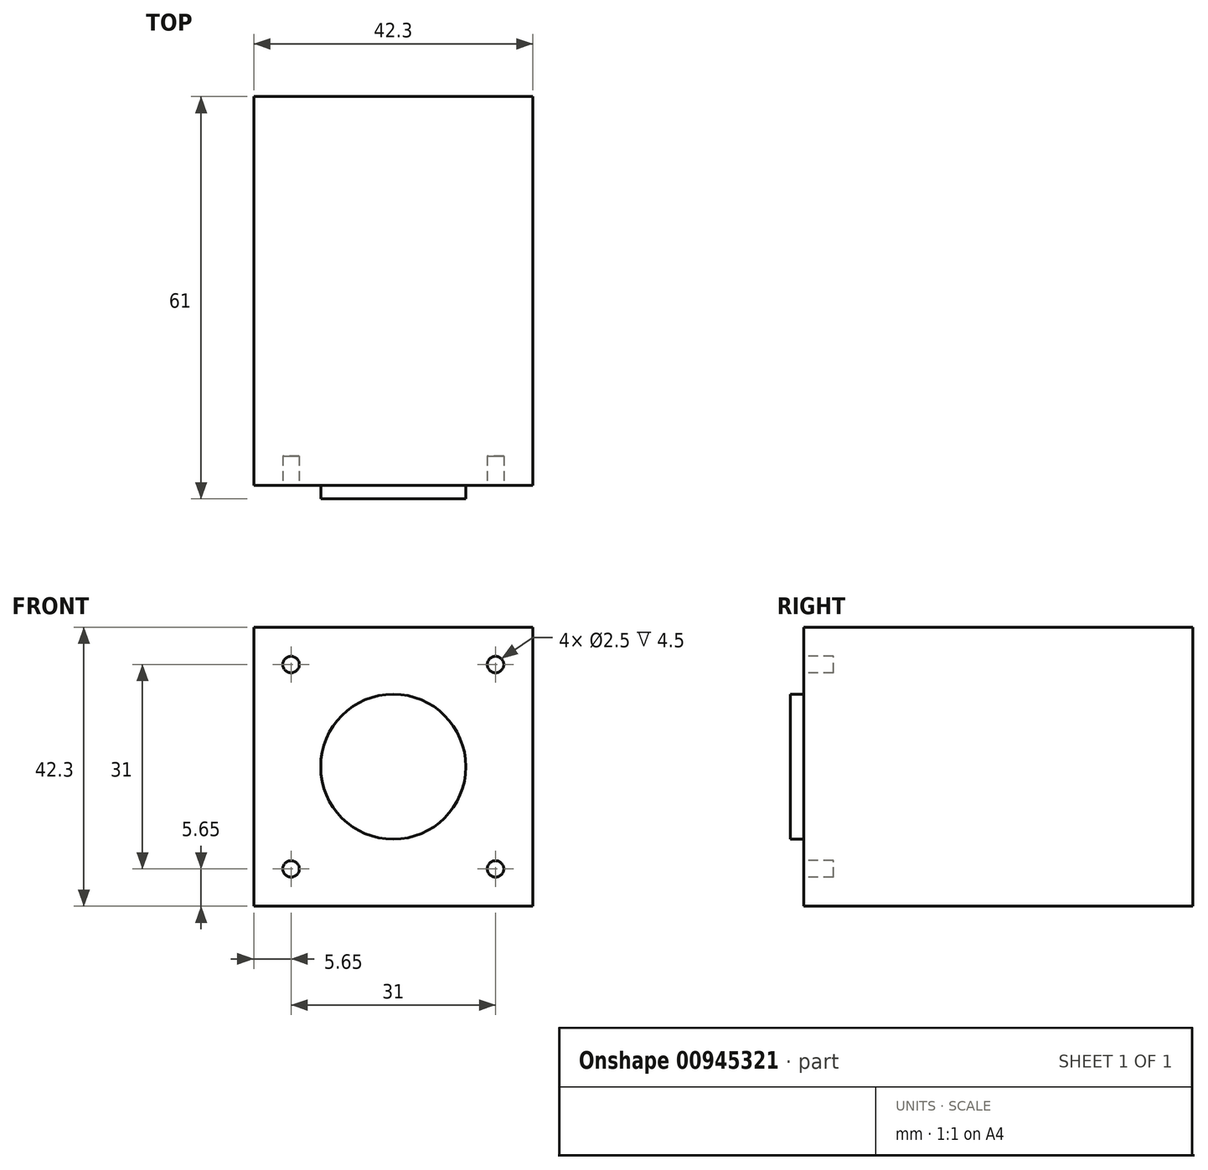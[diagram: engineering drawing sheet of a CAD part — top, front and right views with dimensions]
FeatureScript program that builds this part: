
annotation { "Feature Type Name" : "Feature", "Feature Type Description" : "" }
export const myFeature = defineFeature(function(context is Context, id is Id, definition is map)
    precondition{}
    {
        {
            var Q0;
            Q0=qCreatedBy(makeId("Front.planeOp"),FACE);
            var sketch = newSketch(context, id + "F0", { "sketchPlane" : qUnion([Q0])});
            skLineSegment(sketch, "E0.bottom", {"start": v(-21.15, 21.15) * mm, "end": v(21.15, 21.15) * mm});
            skLineSegment(sketch, "E0.top", {"start": v(-21.15, -21.15) * mm, "end": v(21.15, -21.15) * mm});
            skLineSegment(sketch, "E0.left", {"start": v(-21.15, 21.15) * mm, "end": v(-21.15, -21.15) * mm});
            skLineSegment(sketch, "E0.right", {"start": v(21.15, 21.15) * mm, "end": v(21.15, -21.15) * mm});
            skPoint(sketch, "E1", {"position": v(0, 0) * mm});
            skSolve(sketch);
        }
        {
            var Q0;
            Q0=makeQuery(id+"F0.imprint","IMPRINT",FACE,{"disambiguationData":[TD([[makeQuery(id+"F0.imprint","IMPRINT",EDGE,{"derivedFrom":sQuery(id+"F0.wireOp",EDGE,"E0.bottom")}),-1.0]])]});
            extrude(context, id + "F1", {"entities" : qUnion([Q0]), "depth" : 59 * mm});
        }
        {
            var Q0;
            Q0=makeQuery(id+"F1.opExtrude","CAP_FACE",FACE,{"disambiguationData":[OSD([sQuery(id+"F0.wireOp",EDGE,"E0.bottom"),sQuery(id+"F0.wireOp",EDGE,"E0.top"),sQuery(id+"F0.wireOp",EDGE,"E0.left"),sQuery(id+"F0.wireOp",EDGE,"E0.right")])],"isStart":false});
            var sketch = newSketch(context, id + "F2", { "sketchPlane" : qUnion([Q0])});
            skCircle(sketch, "E2", {"center": v(0, 0) * mm, "radius": 11 * mm});
            skSolve(sketch);
        }
        {
            var Q0;
            Q0=makeQuery(id+"F2.imprint","IMPRINT",FACE,{"disambiguationData":[TD([[makeQuery(id+"F2.imprint","IMPRINT",EDGE,{"derivedFrom":sQuery(id+"F2.wireOp",EDGE,"E2")}),1.0]])]});
            extrude(context, id + "F3", {"entities" : qUnion([Q0]), "operationType" : NewBodyOperationType.ADD, "depth" : 2 * mm});
        }
        {
            var Q0;
            Q0=makeQuery(id+"F3.opExtrude","CAP_FACE",FACE,{"disambiguationData":[OSD([sQuery(id+"F2.wireOp",EDGE,"E2")])],"isStart":false});
            var sketch = newSketch(context, id + "F4", { "sketchPlane" : qUnion([Q0])});
            skCircle(sketch, "E3", {"center": v(0, 0) * mm, "radius": 2.5 * mm});
            skSolve(sketch);
        }
        {
            var Q0;
            Q0=makeQuery(id+"F4.imprint","IMPRINT",FACE,{"disambiguationData":[TD([[makeQuery(id+"F4.imprint","IMPRINT",EDGE,{"derivedFrom":sQuery(id+"F4.wireOp",EDGE,"E3")}),1.0]])]});
            extrude(context, id + "F5", {"entities" : qUnion([Q0]), "operationType" : NewBodyOperationType.ADD, "depth" : 22 * mm});
        }
        {
            var Q0;
            Q0=makeQuery(id+"F5.opExtrude","CAP_FACE",FACE,{"disambiguationData":[OSD([sQuery(id+"F4.wireOp",EDGE,"E3")])],"isStart":false});
            var sketch = newSketch(context, id + "F6", { "sketchPlane" : qUnion([Q0])});
            skLineSegment(sketch, "E4", {"start": v(-1.5, 2) * mm, "end": v(1.5, 2) * mm});
            skLineSegment(sketch, "E5", {"start": v(0, 2.5) * mm, "end": v(0, 2) * mm});
            skSolve(sketch);
        }
        {
            var Q0;
            {var subQ3=sQuery(id+"F6.wireOp",EDGE,"E5");Q0=makeQuery(id+"F6.imprint","IMPRINT",FACE,{"disambiguationData":[TD([[makeQuery(id+"F6.imprint","IMPRINT",EDGE,{"derivedFrom":subQ3}),-1.0]])]});}
            var Q1;
            {var subQ3=sQuery(id+"F6.wireOp",EDGE,"E5");Q1=makeQuery(id+"F6.imprint","IMPRINT",FACE,{"disambiguationData":[TD([[makeQuery(id+"F6.imprint","IMPRINT",EDGE,{"derivedFrom":subQ3}),1.0]])]});}
            extrude(context, id + "F7", {"entities" : qUnion([Q0, Q1]), "operationType" : NewBodyOperationType.REMOVE, "oppositeDirection" : true, "depth" : 15 * mm});
        }
        {
            var Q0;
            Q0=makeQuery(id+"F1.opExtrude","CAP_FACE",FACE,{"disambiguationData":[OSD([sQuery(id+"F0.wireOp",EDGE,"E0.bottom"),sQuery(id+"F0.wireOp",EDGE,"E0.top"),sQuery(id+"F0.wireOp",EDGE,"E0.left"),sQuery(id+"F0.wireOp",EDGE,"E0.right")])],"isStart":false});
            var sketch = newSketch(context, id + "F8", { "sketchPlane" : qUnion([Q0])});
            skLineSegment(sketch, "E6.bottom", {"start": v(-15.5, 15.5) * mm, "end": v(15.5, 15.5) * mm});
            skLineSegment(sketch, "E6.top", {"start": v(-15.5, -15.5) * mm, "end": v(15.5, -15.5) * mm});
            skLineSegment(sketch, "E6.left", {"start": v(-15.5, 15.5) * mm, "end": v(-15.5, -15.5) * mm});
            skLineSegment(sketch, "E6.right", {"start": v(15.5, 15.5) * mm, "end": v(15.5, -15.5) * mm});
            skPoint(sketch, "E7", {"position": v(0, 0) * mm});
            skCircle(sketch, "E8", {"center": v(-15.5, 15.5) * mm, "radius": 1.25 * mm});
            skCircle(sketch, "E9", {"center": v(15.5, 15.5) * mm, "radius": 1.25 * mm});
            skCircle(sketch, "E10", {"center": v(-15.5, -15.5) * mm, "radius": 1.25 * mm});
            skCircle(sketch, "E11", {"center": v(15.5, -15.5) * mm, "radius": 1.25 * mm});
            skSolve(sketch);
        }
        {
            var Q0;
            {var subQ0=sQuery(id+"F8.wireOp",EDGE,"E6.right");var subQ1=sQuery(id+"F8.wireOp",EDGE,"E6.bottom");var subQ2=makeQuery(id+"F8.imprint","INTERSECT",VERTEX,{"derivedFrom":[subQ1,subQ0]});Q0=makeQuery(id+"F8.imprint","IMPRINT",FACE,{"disambiguationData":[TD([[makeQuery(id+"F8.imprint","IMPRINT",EDGE,{"disambiguationData":[TD([[subQ2,1.0]])],"derivedFrom":subQ1}),1.0]])]});}
            var Q1;
            {var subQ0=sQuery(id+"F8.wireOp",EDGE,"E6.right");var subQ1=sQuery(id+"F8.wireOp",EDGE,"E6.bottom");var subQ2=makeQuery(id+"F8.imprint","INTERSECT",VERTEX,{"derivedFrom":[subQ1,subQ0]});Q1=makeQuery(id+"F8.imprint","IMPRINT",FACE,{"disambiguationData":[TD([[makeQuery(id+"F8.imprint","IMPRINT",EDGE,{"disambiguationData":[TD([[subQ2,1.0]])],"derivedFrom":subQ1}),-1.0]])]});}
            var Q2;
            {var subQ0=sQuery(id+"F8.wireOp",EDGE,"E6.left");var subQ1=sQuery(id+"F8.wireOp",EDGE,"E6.bottom");var subQ2=makeQuery(id+"F8.imprint","INTERSECT",VERTEX,{"derivedFrom":[subQ1,subQ0]});Q2=makeQuery(id+"F8.imprint","IMPRINT",FACE,{"disambiguationData":[TD([[makeQuery(id+"F8.imprint","IMPRINT",EDGE,{"disambiguationData":[TD([[subQ2,-1.0]])],"derivedFrom":subQ1}),1.0]])]});}
            var Q3;
            {var subQ0=sQuery(id+"F8.wireOp",EDGE,"E6.left");var subQ1=sQuery(id+"F8.wireOp",EDGE,"E6.bottom");var subQ2=makeQuery(id+"F8.imprint","INTERSECT",VERTEX,{"derivedFrom":[subQ1,subQ0]});Q3=makeQuery(id+"F8.imprint","IMPRINT",FACE,{"disambiguationData":[TD([[makeQuery(id+"F8.imprint","IMPRINT",EDGE,{"disambiguationData":[TD([[subQ2,-1.0]])],"derivedFrom":subQ1}),-1.0]])]});}
            var Q4;
            {var subQ0=sQuery(id+"F8.wireOp",EDGE,"E6.left");var subQ1=sQuery(id+"F8.wireOp",EDGE,"E6.top");var subQ2=makeQuery(id+"F8.imprint","INTERSECT",VERTEX,{"derivedFrom":[subQ1,subQ0]});Q4=makeQuery(id+"F8.imprint","IMPRINT",FACE,{"disambiguationData":[TD([[makeQuery(id+"F8.imprint","IMPRINT",EDGE,{"disambiguationData":[TD([[subQ2,-1.0]])],"derivedFrom":subQ1}),-1.0]])]});}
            var Q5;
            {var subQ0=sQuery(id+"F8.wireOp",EDGE,"E6.left");var subQ1=sQuery(id+"F8.wireOp",EDGE,"E6.top");var subQ2=makeQuery(id+"F8.imprint","INTERSECT",VERTEX,{"derivedFrom":[subQ1,subQ0]});Q5=makeQuery(id+"F8.imprint","IMPRINT",FACE,{"disambiguationData":[TD([[makeQuery(id+"F8.imprint","IMPRINT",EDGE,{"disambiguationData":[TD([[subQ2,-1.0]])],"derivedFrom":subQ1}),1.0]])]});}
            var Q6;
            {var subQ0=sQuery(id+"F8.wireOp",EDGE,"E6.right");var subQ1=sQuery(id+"F8.wireOp",EDGE,"E6.top");var subQ2=makeQuery(id+"F8.imprint","INTERSECT",VERTEX,{"derivedFrom":[subQ1,subQ0]});Q6=makeQuery(id+"F8.imprint","IMPRINT",FACE,{"disambiguationData":[TD([[makeQuery(id+"F8.imprint","IMPRINT",EDGE,{"disambiguationData":[TD([[subQ2,1.0]])],"derivedFrom":subQ1}),1.0]])]});}
            var Q7;
            {var subQ0=sQuery(id+"F8.wireOp",EDGE,"E6.right");var subQ1=sQuery(id+"F8.wireOp",EDGE,"E6.top");var subQ2=makeQuery(id+"F8.imprint","INTERSECT",VERTEX,{"derivedFrom":[subQ1,subQ0]});Q7=makeQuery(id+"F8.imprint","IMPRINT",FACE,{"disambiguationData":[TD([[makeQuery(id+"F8.imprint","IMPRINT",EDGE,{"disambiguationData":[TD([[subQ2,1.0]])],"derivedFrom":subQ1}),-1.0]])]});}
            extrude(context, id + "F9", {"entities" : qUnion([Q0, Q1, Q2, Q3, Q4, Q5, Q6, Q7]), "operationType" : NewBodyOperationType.REMOVE, "oppositeDirection" : true, "depth" : 4.5 * mm});
        }
        {
            var Q0;
            Q0=makeQuery(id+"F5.opExtrude","CAP_FACE",FACE,{"disambiguationData":[OSD([sQuery(id+"F4.wireOp",EDGE,"E3")])],"isStart":false});
            extrude(context, id + "F10", {"entities" : qUnion([Q0]), "operationType" : NewBodyOperationType.REMOVE, "oppositeDirection" : true, "depth" : 22 * mm, "offsetDistance" : 25 * mm});
        }
        {
            var Q0;
            Q0=makeQuery(id+"F7.boolean.opBoolean","COPY",FACE,{"derivedFrom":makeQuery(id+"F7.opExtrude","CAP_FACE",FACE,{"disambiguationData":[OSD([sQuery(id+"F4.wireOp",EDGE,"E3"),sQuery(id+"F6.wireOp",EDGE,"E4")])],"isStart":false})});
            extrude(context, id + "F11", {"entities" : qUnion([Q0]), "operationType" : NewBodyOperationType.REMOVE, "oppositeDirection" : true, "depth" : 7 * mm, "offsetDistance" : 25 * mm});
        }
    });
